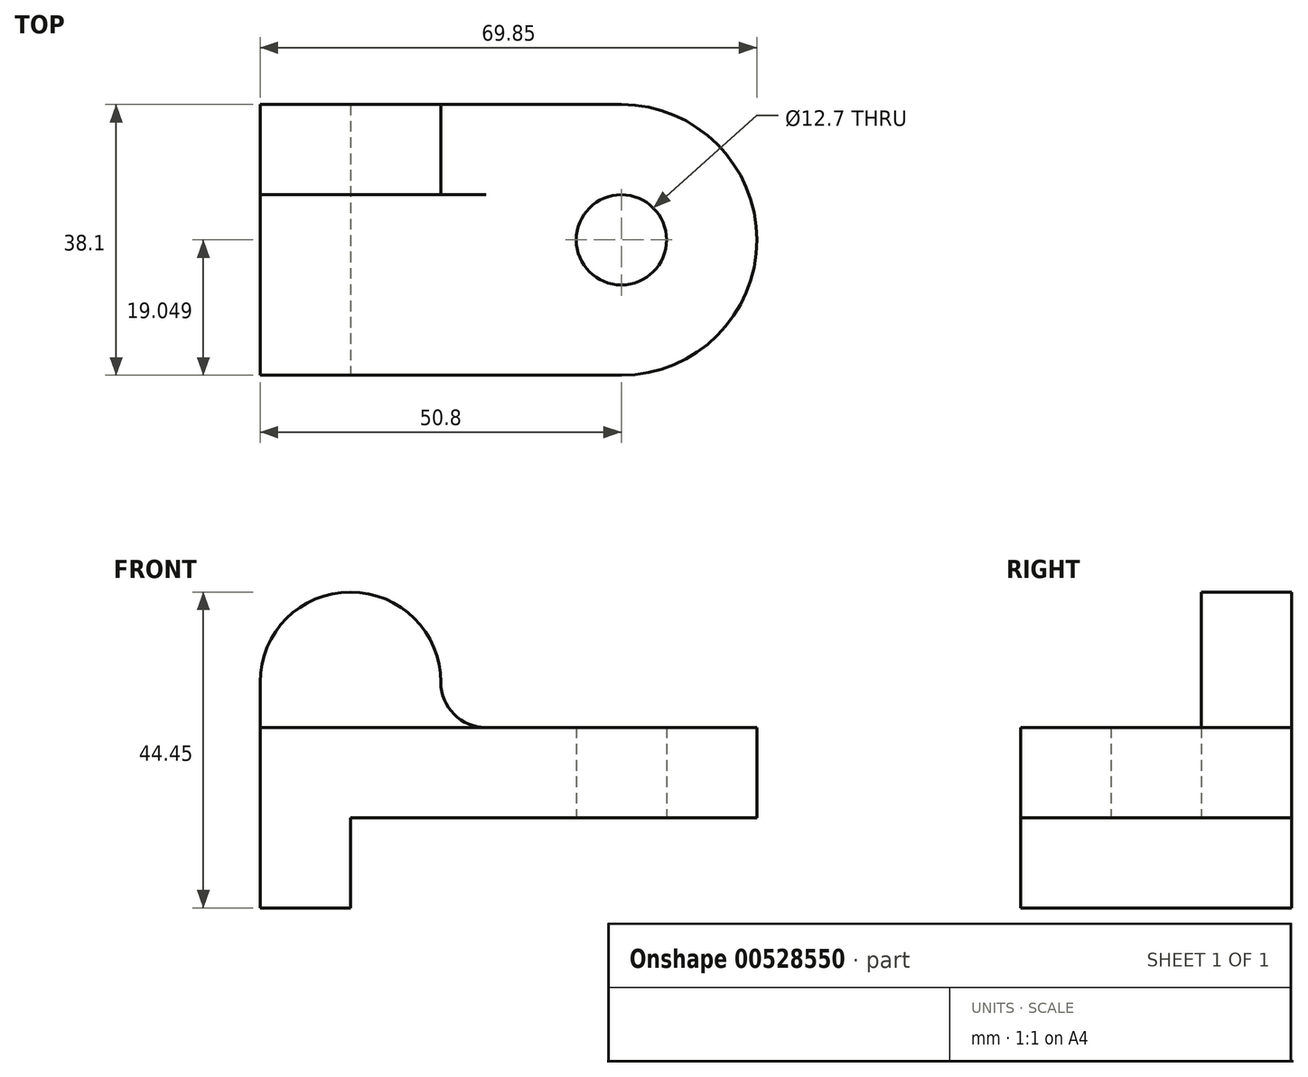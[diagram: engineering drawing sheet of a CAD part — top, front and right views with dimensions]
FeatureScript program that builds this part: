
annotation { "Feature Type Name" : "Feature", "Feature Type Description" : "" }
export const myFeature = defineFeature(function(context is Context, id is Id, definition is map)
    precondition{}
    {
        {
            var Q0;
            Q0=qCreatedBy(makeId("Top.planeOp"),FACE);
            var sketch = newSketch(context, id + "F0", { "sketchPlane" : qUnion([Q0])});
            skLineSegment(sketch, "E0", {"start": v(0, 20.82) * mm, "end": v(-50.8, 20.82) * mm});
            skLineSegment(sketch, "E1", {"start": v(-50.8, 20.82) * mm, "end": v(-50.8, -17.28) * mm});
            skLineSegment(sketch, "E2", {"start": v(-50.8, -17.28) * mm, "end": v(0, -17.28) * mm});
            skArc(sketch, "E3", {"start": v(0, -17.28) * mm, "mid": v(19.05, 1.77) * mm, "end": v(0, 20.82) * mm});
            skLineSegment(sketch, "E4", {"start": v(-50.8, 8.12) * mm, "end": v(-25.4, 8.12) * mm});
            skLineSegment(sketch, "E5", {"start": v(-25.4, 8.12) * mm, "end": v(-25.4, 20.82) * mm});
            skLineSegment(sketch, "E6", {"start": v(-38.1, 20.82) * mm, "end": v(-38.1, -17.28) * mm});
            skCircle(sketch, "E7", {"center": v(0, 1.77) * mm, "radius": 6.35 * mm});
            skSolve(sketch);
        }
        {
            var Q0;
            {var subQ4=sQuery(id+"F0.wireOp",EDGE,"E3");Q0=makeQuery(id+"F0.imprint","IMPRINT",FACE,{"disambiguationData":[TD([[makeQuery(id+"F0.imprint","IMPRINT",EDGE,{"derivedFrom":subQ4}),1.0]])]});}
            var Q1;
            {var subQ0=sQuery(id+"F0.wireOp",EDGE,"E2");var subQ1=sQuery(id+"F0.wireOp",EDGE,"E1");var subQ2=makeQuery(id+"F0.imprint","INTERSECT",VERTEX,{"derivedFrom":[subQ1,subQ0]});Q1=makeQuery(id+"F0.imprint","IMPRINT",FACE,{"disambiguationData":[TD([[makeQuery(id+"F0.imprint","IMPRINT",EDGE,{"disambiguationData":[TD([[subQ2,1.0]])],"derivedFrom":subQ1}),1.0]])]});}
            var Q2;
            {var subQ0=sQuery(id+"F0.wireOp",EDGE,"E1");var subQ1=sQuery(id+"F0.wireOp",EDGE,"E0");var subQ2=makeQuery(id+"F0.imprint","INTERSECT",VERTEX,{"derivedFrom":[subQ1,subQ0]});Q2=makeQuery(id+"F0.imprint","IMPRINT",FACE,{"disambiguationData":[TD([[makeQuery(id+"F0.imprint","IMPRINT",EDGE,{"disambiguationData":[TD([[subQ2,1.0]])],"derivedFrom":subQ1}),1.0]])]});}
            var Q3;
            {var subQ0=sQuery(id+"F0.wireOp",EDGE,"E5");Q3=makeQuery(id+"F0.imprint","IMPRINT",FACE,{"disambiguationData":[TD([[makeQuery(id+"F0.imprint","IMPRINT",EDGE,{"derivedFrom":subQ0}),1.0]])]});}
            extrude(context, id + "F1", {"entities" : qUnion([Q0, Q1, Q2, Q3]), "depth" : 12.7 * mm, "offsetDistance" : 25.4 * mm});
        }
        {
            var Q0;
            {var subQ0=sQuery(id+"F0.wireOp",EDGE,"E2");var subQ1=sQuery(id+"F0.wireOp",EDGE,"E1");var subQ2=makeQuery(id+"F0.imprint","INTERSECT",VERTEX,{"derivedFrom":[subQ1,subQ0]});Q0=makeQuery(id+"F0.imprint","IMPRINT",FACE,{"disambiguationData":[TD([[makeQuery(id+"F0.imprint","IMPRINT",EDGE,{"disambiguationData":[TD([[subQ2,1.0]])],"derivedFrom":subQ1}),1.0]])]});}
            var Q1;
            {var subQ0=sQuery(id+"F0.wireOp",EDGE,"E1");var subQ1=sQuery(id+"F0.wireOp",EDGE,"E0");var subQ2=makeQuery(id+"F0.imprint","INTERSECT",VERTEX,{"derivedFrom":[subQ1,subQ0]});Q1=makeQuery(id+"F0.imprint","IMPRINT",FACE,{"disambiguationData":[TD([[makeQuery(id+"F0.imprint","IMPRINT",EDGE,{"disambiguationData":[TD([[subQ2,1.0]])],"derivedFrom":subQ1}),1.0]])]});}
            extrude(context, id + "F2", {"entities" : qUnion([Q0, Q1]), "operationType" : NewBodyOperationType.ADD, "oppositeDirection" : true, "depth" : 12.7 * mm, "offsetDistance" : 25.4 * mm});
        }
        {
            var Q0;
            {var subQ0=sQuery(id+"F0.wireOp",EDGE,"E5");Q0=makeQuery(id+"F0.imprint","IMPRINT",FACE,{"disambiguationData":[TD([[makeQuery(id+"F0.imprint","IMPRINT",EDGE,{"derivedFrom":subQ0}),1.0]])]});}
            extrude(context, id + "F3", {"entities" : qUnion([Q0]), "operationType" : NewBodyOperationType.ADD, "depth" : 19.05 * mm, "offsetDistance" : 25.4 * mm});
        }
        {
            var Q0;
            Q0=makeQuery(id+"F3.opExtrude","SWEPT_FACE",FACE,{"disambiguationData":[OSD([sQuery(id+"F0.wireOp",EDGE,"E6")])]});
            extrude(context, id + "F4", {"entities" : qUnion([Q0]), "operationType" : NewBodyOperationType.ADD, "depth" : 12.7 * mm, "offsetDistance" : 25.4 * mm});
        }
        {
            var Q0;
            {var subQ0=sQuery(id+"F0.wireOp",EDGE,"E4");Q0=makeQuery(id+"F4.boolean.opBoolean","MERGE",FACE,{"derivedFrom":[makeQuery(id+"F3.opExtrude","SWEPT_FACE",FACE,{"disambiguationData":[OSD([subQ0])]}),makeQuery(id+"F4.opExtrude","SWEPT_FACE",FACE,{"disambiguationData":[OSD([subQ0,sQuery(id+"F0.wireOp",EDGE,"E6")])]})]});}
            var sketch = newSketch(context, id + "F5", { "sketchPlane" : qUnion([Q0])});
            skArc(sketch, "E8", {"start": v(-25.4, 19.05) * mm, "mid": v(-38.1, 31.75) * mm, "end": v(-50.8, 19.05) * mm});
            skSolve(sketch);
        }
        {
            var Q0;
            Q0=makeQuery(id+"F5.imprint","IMPRINT",FACE,{"disambiguationData":[TD([[makeQuery(id+"F5.imprint","IMPRINT",EDGE,{"derivedFrom":sQuery(id+"F5.wireOp",EDGE,"E8")}),1.0]])]});
            extrude(context, id + "F6", {"entities" : qUnion([Q0]), "operationType" : NewBodyOperationType.ADD, "oppositeDirection" : true, "depth" : 12.7 * mm, "offsetDistance" : 25.4 * mm});
        }
        {
            var Q0;
            Q0=makeQuery(id+"F3.boolean.opBoolean","INTERSECT",EDGE,{"derivedFrom":[makeQuery(id+"F1.opExtrude","CAP_FACE",FACE,{"disambiguationData":[OSD([sQuery(id+"F0.wireOp",EDGE,"E0"),sQuery(id+"F0.wireOp",EDGE,"E1"),sQuery(id+"F0.wireOp",EDGE,"E2"),sQuery(id+"F0.wireOp",EDGE,"E3"),sQuery(id+"F0.wireOp",EDGE,"E7")])],"isStart":false}),makeQuery(id+"F3.opExtrude","SWEPT_FACE",FACE,{"disambiguationData":[OSD([sQuery(id+"F0.wireOp",EDGE,"E5")])]})]});
            fillet(context, id + "F7", {"entities" : qUnion([Q0]), "radius" : 6.35 * mm, "tangentPropagation" : true, "allowEdgeOverflow" : false});
        }
    });
